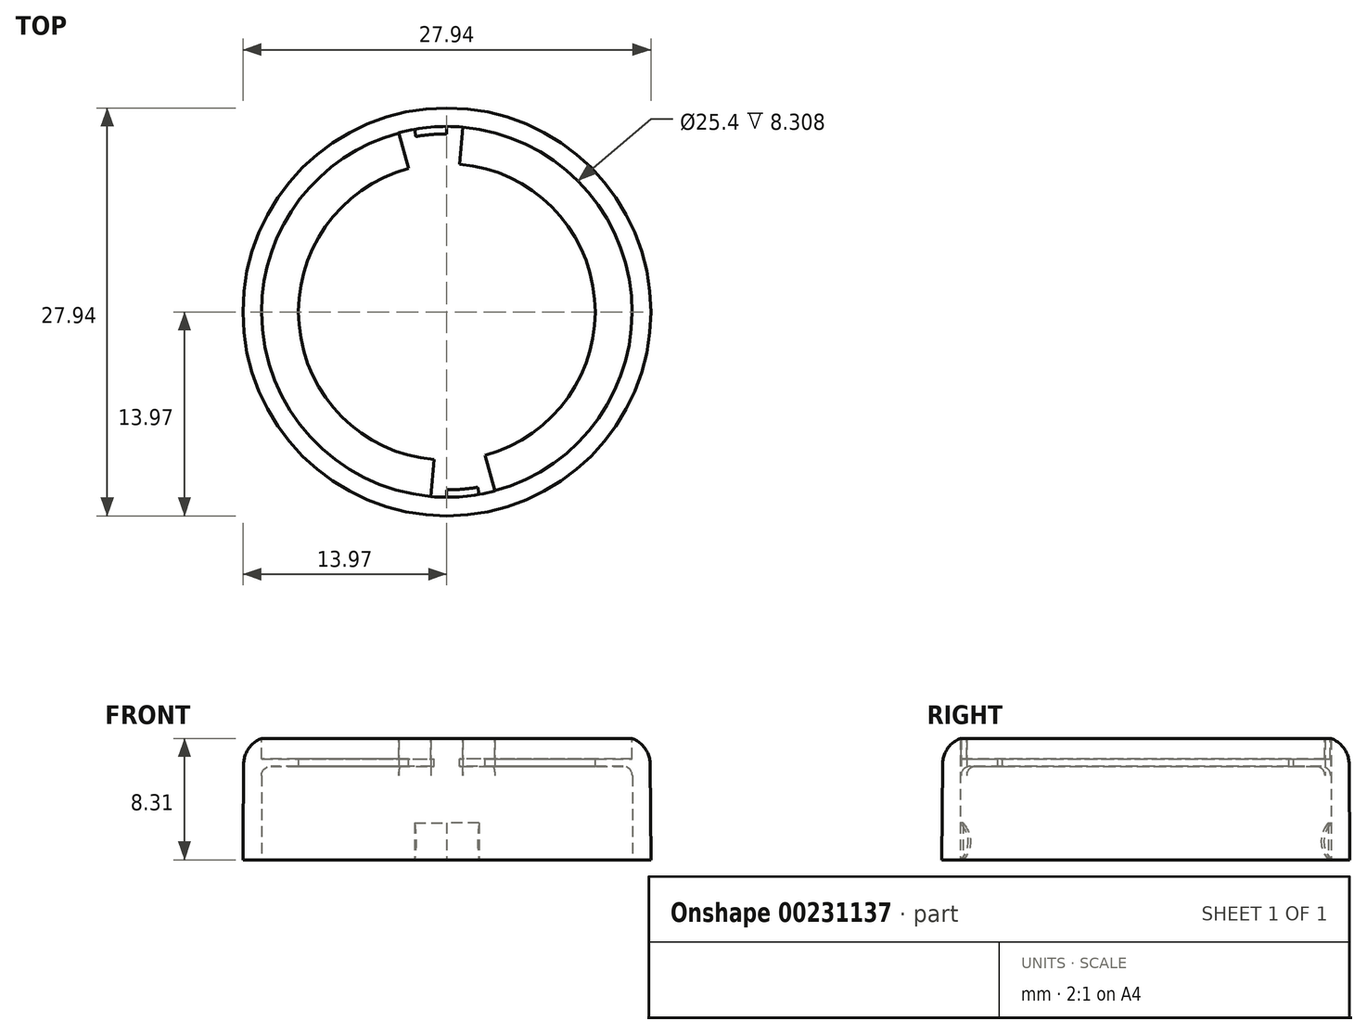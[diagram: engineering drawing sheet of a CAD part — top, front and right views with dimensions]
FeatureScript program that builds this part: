
annotation { "Feature Type Name" : "Feature", "Feature Type Description" : "" }
export const myFeature = defineFeature(function(context is Context, id is Id, definition is map)
    precondition{}
    {
        {
            var Q0;
            Q0=qCreatedBy(makeId("Front.planeOp"),FACE);
            var sketch = newSketch(context, id + "F0", { "sketchPlane" : qUnion([Q0])});
            skLineSegment(sketch, "E0", {"start": v(-12.7, 0) * mm, "end": v(-12.7, 5.77) * mm});
            skLineSegment(sketch, "E1", {"start": v(-12.07, 6.4) * mm, "end": v(0, 6.4) * mm});
            skLineSegment(sketch, "E2", {"start": v(0, 6.4) * mm, "end": v(0, 8.44) * mm});
            skLineSegment(sketch, "E3", {"start": v(0, 8.44) * mm, "end": v(-12.01, 8.44) * mm});
            skLineSegment(sketch, "E4", {"start": v(-13.97, 0) * mm, "end": v(-12.7, 0) * mm});
            skLineSegment(sketch, "E5", {"start": v(-13.92, 6.55) * mm, "end": v(-13.97, 0) * mm});
            skPoint(sketch, "E6.visualSharp", {"position": v(-13.9, 8.44) * mm});
            skArc(sketch, "E6.filletArc", {"start": v(-12.01, 8.44) * mm, "mid": v(-13.36, 7.88) * mm, "end": v(-13.92, 6.55) * mm});
            skPoint(sketch, "E7.visualSharp", {"position": v(-12.7, 6.4) * mm});
            skArc(sketch, "E7.filletArc", {"start": v(-12.07, 6.4) * mm, "mid": v(-12.51, 6.22) * mm, "end": v(-12.7, 5.77) * mm});
            skSolve(sketch);
        }
        {
            var Q0;
            Q0=makeQuery(id+"F0.imprint","IMPRINT",FACE,{"disambiguationData":[TD([[makeQuery(id+"F0.imprint","IMPRINT",EDGE,{"derivedFrom":sQuery(id+"F0.wireOp",EDGE,"E0")}),1.0]])]});
            var Q1;
            Q1=sQuery(id+"F0.wireOp",EDGE,"E2");
            revolve(context, id + "F1", {"entities" : qUnion([Q0]), "axis" : qUnion([Q1]), "revolveType" : RevolveType.FULL});
        }
        {
            var Q0;
            Q0=makeQuery(id+"F1.opRevolve","SWEPT_FACE",FACE,{"disambiguationData":[OSD([sQuery(id+"F0.wireOp",EDGE,"E3")])]});
            var sketch = newSketch(context, id + "F2", { "sketchPlane" : qUnion([Q0])});
            skCircle(sketch, "E8", {"center": v(0, 0) * mm, "radius": 12.69 * mm});
            skSolve(sketch);
        }
        {
            var Q0;
            Q0=qSketchRegion(id+"F2",true);
            extrude(context, id + "F3", {"entities" : qUnion([Q0]), "operationType" : NewBodyOperationType.REMOVE, "oppositeDirection" : true, "depth" : 1.52 * mm});
        }
        {
            var Q0;
            Q0=makeQuery(id+"F3.boolean.opBoolean","COPY",FACE,{"derivedFrom":makeQuery(id+"F3.opExtrude","CAP_FACE",FACE,{"disambiguationData":[OSD([sQuery(id+"F2.wireOp",EDGE,"E8")])],"isStart":false})});
            var sketch = newSketch(context, id + "F4", { "sketchPlane" : qUnion([Q0])});
            skCircle(sketch, "E9", {"center": v(0, 0) * mm, "radius": 10.16 * mm});
            skSolve(sketch);
        }
        {
            var Q0;
            Q0=qSketchRegion(id+"F4",true);
            extrude(context, id + "F5", {"entities" : qUnion([Q0]), "operationType" : NewBodyOperationType.REMOVE, "oppositeDirection" : true, "depth" : 25.4 * mm});
        }
        {
            var Q0;
            Q0=qCreatedBy(makeId("Right.planeOp"),FACE);
            var sketch = newSketch(context, id + "F6", { "sketchPlane" : qUnion([Q0])});
            skFitSpline(sketch, "E10", {"points": [v(-12.7, 2.54) * mm, v(-12.2, 1.27) * mm, v(-12.7, 0) * mm], "startDerivative": vector(2, -2.68) * mm, "endDerivative": vector(-2.07, -1.98) * mm});
            skFitSpline(sketch, "E11", {"points": [v(12.7, 2.54) * mm, v(12.2, 1.27) * mm, v(12.7, 0) * mm], "startDerivative": vector(-1.7, -1.76) * mm, "endDerivative": vector(1.79, -1.76) * mm});
            skLineSegment(sketch, "E12", {"start": v(0, 0) * mm, "end": v(0, 5.68) * mm});
            skLineSegment(sketch, "E13", {"start": v(-12.7, 2.54) * mm, "end": v(-12.7, 0) * mm});
            skLineSegment(sketch, "E14", {"start": v(12.7, 2.54) * mm, "end": v(12.7, 0) * mm});
            skSolve(sketch);
        }
        {
            var Q0;
            Q0 = qSketchRegion(id + "F6", true);
            var Q1;
            Q1=sQuery(id+"F6.wireOp",EDGE,"E12");
            revolve(context, id + "F7", {"operationType" : NewBodyOperationType.ADD, "entities" : qUnion([Q0]), "axis" : qUnion([Q1]), "revolveType" : RevolveType.ONE_DIRECTION, "angle" : 10 * degree});
        }
        {
            var Q0;
            Q0=qCreatedBy(makeId("Right.planeOp"),FACE);
            var sketch = newSketch(context, id + "F8", { "sketchPlane" : qUnion([Q0])});
            skLineSegment(sketch, "E15.right", {"start": v(0, 5.77) * mm, "end": v(0, 8.31) * mm});
            skLineSegment(sketch, "E16.bottom", {"start": v(0, 8.31) * mm, "end": v(12.7, 8.31) * mm});
            skLineSegment(sketch, "E16.top", {"start": v(0, 5.77) * mm, "end": v(12.7, 5.77) * mm});
            skLineSegment(sketch, "E16.left", {"start": v(0, 8.31) * mm, "end": v(0, 5.77) * mm});
            skLineSegment(sketch, "E16.right", {"start": v(12.7, 8.31) * mm, "end": v(12.7, 5.77) * mm});
            skSolve(sketch);
        }
        {
            var Q0;
            Q0=makeQuery(id+"F8.imprint","IMPRINT",FACE,{"disambiguationData":[TD([[makeQuery(id+"F8.imprint","IMPRINT",EDGE,{"derivedFrom":sQuery(id+"F8.wireOp",EDGE,"E16.bottom")}),-1.0]])]});
            var Q1;
            Q1=sQuery(id+"F8.wireOp",EDGE,"E16.left");
            revolve(context, id + "F9", {"operationType" : NewBodyOperationType.REMOVE, "entities" : qUnion([Q0]), "axis" : qUnion([Q1]), "revolveType" : RevolveType.TWO_DIRECTIONS, "oppositeDirection" : true, "angle" : 15 * degree, "angleBack" : 355 * degree});
        }
        {
            var Q0;
            Q0=qCreatedBy(makeId("Right.planeOp"),FACE);
            var sketch = newSketch(context, id + "F10", { "sketchPlane" : qUnion([Q0])});
            skLineSegment(sketch, "E17.bottom", {"start": v(0, 8.31) * mm, "end": v(-12.7, 8.31) * mm});
            skLineSegment(sketch, "E17.top", {"start": v(0, 5.77) * mm, "end": v(-12.7, 5.77) * mm});
            skLineSegment(sketch, "E17.left", {"start": v(0, 8.31) * mm, "end": v(0, 5.77) * mm});
            skLineSegment(sketch, "E17.right", {"start": v(-12.7, 8.31) * mm, "end": v(-12.7, 5.77) * mm});
            skSolve(sketch);
        }
        {
            var Q0;
            Q0 = qSketchRegion(id + "F10", true);
            var Q1;
            Q1=sQuery(id+"F10.wireOp",EDGE,"E17.left");
            revolve(context, id + "F11", {"operationType" : NewBodyOperationType.REMOVE, "entities" : qUnion([Q0]), "axis" : qUnion([Q1]), "revolveType" : RevolveType.TWO_DIRECTIONS, "oppositeDirection" : true, "angle" : 15 * degree, "angleBack" : 355 * degree});
        }
    });
